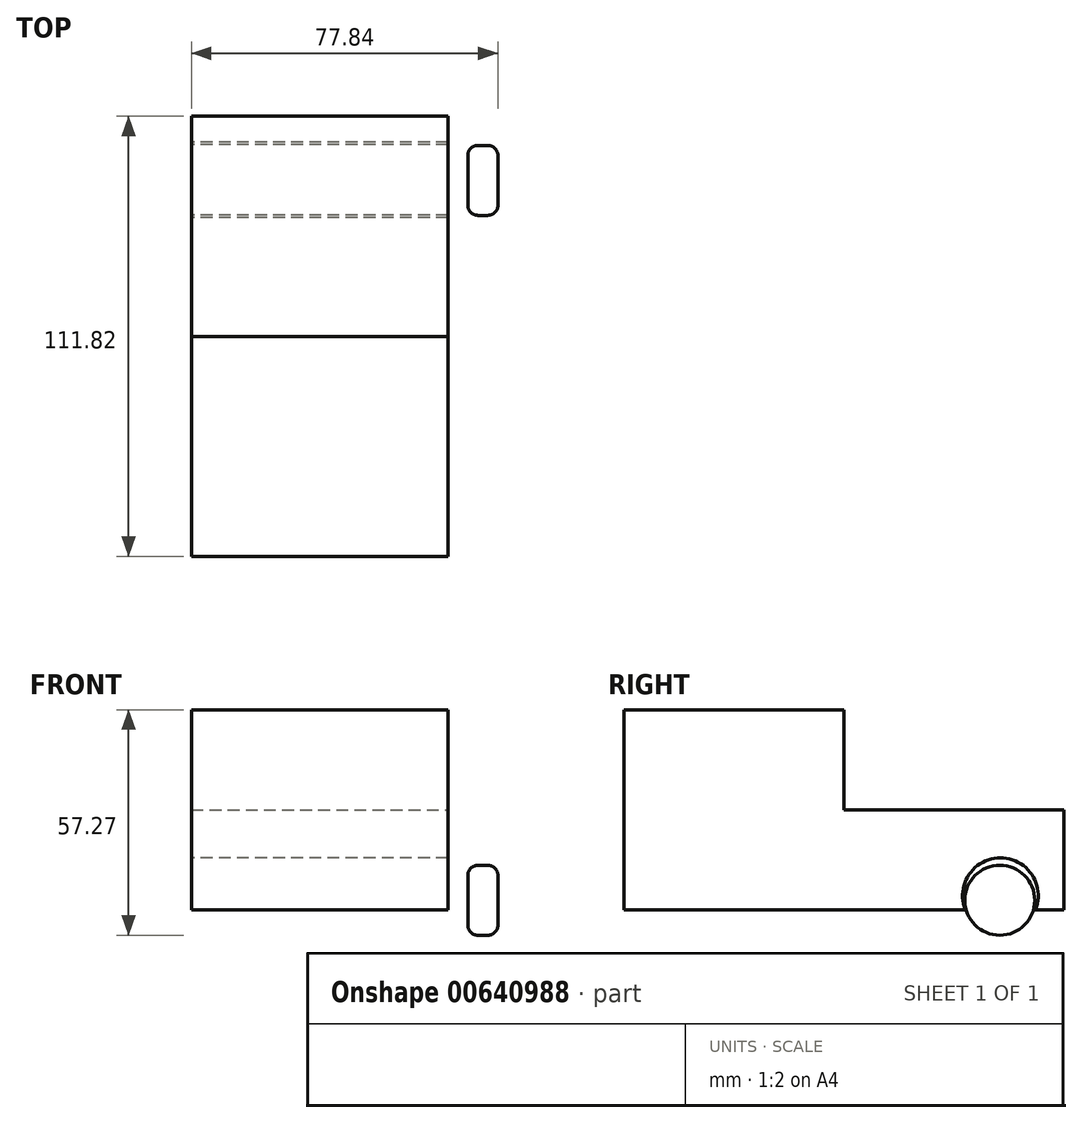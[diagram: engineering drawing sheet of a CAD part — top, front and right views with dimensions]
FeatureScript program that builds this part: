
annotation { "Feature Type Name" : "Feature", "Feature Type Description" : "" }
export const myFeature = defineFeature(function(context is Context, id is Id, definition is map)
    precondition{}
    {
        {
            var Q0;
            Q0=qCreatedBy(makeId("Top.planeOp"),FACE);
            var sketch = newSketch(context, id + "F0", { "sketchPlane" : qUnion([Q0])});
            skLineSegment(sketch, "E0.bottom", {"start": v(-70.22, 55.69) * mm, "end": v(-5.06, 55.69) * mm});
            skLineSegment(sketch, "E0.top", {"start": v(-70.22, -56.13) * mm, "end": v(-5.06, -56.13) * mm});
            skLineSegment(sketch, "E0.left", {"start": v(-70.22, 55.69) * mm, "end": v(-70.22, -56.13) * mm});
            skLineSegment(sketch, "E0.right", {"start": v(-5.06, 55.69) * mm, "end": v(-5.06, -56.13) * mm});
            skSolve(sketch);
        }
        {
            var Q0;
            Q0=makeQuery(id+"F0.imprint","IMPRINT",FACE,{"disambiguationData":[TD([[makeQuery(id+"F0.imprint","IMPRINT",EDGE,{"derivedFrom":sQuery(id+"F0.wireOp",EDGE,"E0.bottom")}),-1.0]])]});
            extrude(context, id + "F1", {"entities" : qUnion([Q0]), "depth" : 25.4 * mm, "offsetDistance" : 25.4 * mm});
        }
        {
            var Q0;
            Q0=makeQuery(id+"F1.opExtrude","CAP_FACE",FACE,{"disambiguationData":[OSD([sQuery(id+"F0.wireOp",EDGE,"E0.bottom"),sQuery(id+"F0.wireOp",EDGE,"E0.top"),sQuery(id+"F0.wireOp",EDGE,"E0.left"),sQuery(id+"F0.wireOp",EDGE,"E0.right")])],"isStart":false});
            var sketch = newSketch(context, id + "F2", { "sketchPlane" : qUnion([Q0])});
            skLineSegment(sketch, "E1.bottom", {"start": v(-70.22, -0.22) * mm, "end": v(-5.06, -0.22) * mm});
            skLineSegment(sketch, "E1.top", {"start": v(-70.22, -56.13) * mm, "end": v(-5.06, -56.13) * mm});
            skLineSegment(sketch, "E1.left", {"start": v(-70.22, -0.22) * mm, "end": v(-70.22, -56.13) * mm});
            skLineSegment(sketch, "E1.right", {"start": v(-5.06, -0.22) * mm, "end": v(-5.06, -56.13) * mm});
            skSolve(sketch);
        }
        {
            var Q0;
            Q0=makeQuery(id+"F2.imprint","IMPRINT",FACE,{"disambiguationData":[TD([[makeQuery(id+"F2.imprint","IMPRINT",EDGE,{"derivedFrom":sQuery(id+"F2.wireOp",EDGE,"E1.bottom")}),-1.0]])]});
            extrude(context, id + "F3", {"entities" : qUnion([Q0]), "operationType" : NewBodyOperationType.ADD, "depth" : 25.4 * mm, "offsetDistance" : 25.4 * mm});
        }
        {
            var Q0;
            Q0=makeQuery(id+"F3.boolean.opBoolean","MERGE",FACE,{"derivedFrom":[makeQuery(id+"F1.opExtrude","SWEPT_FACE",FACE,{"disambiguationData":[OSD([sQuery(id+"F0.wireOp",EDGE,"E0.left")])]}),makeQuery(id+"F3.opExtrude","SWEPT_FACE",FACE,{"disambiguationData":[OSD([sQuery(id+"F2.wireOp",EDGE,"E1.left")])]})]});
            var sketch = newSketch(context, id + "F4", { "sketchPlane" : qUnion([Q0])});
            skCircle(sketch, "E2", {"center": v(-39.53, 3.58) * mm, "radius": 9.61 * mm});
            skSolve(sketch);
        }
        {
            var Q0;
            {var subQ0=sQuery(id+"F4.wireOp",EDGE,"E2");var subQ1=makeQuery(id+"F1.opExtrude","CAP_EDGE",EDGE,{"disambiguationData":[OSD([sQuery(id+"F0.wireOp",EDGE,"E0.left")])],"isStart":true});var subQ2=makeQuery(id+"F4.imprint","INTERSECT",VERTEX,{"disambiguationData":[OD(0.0)],"derivedFrom":[subQ1,subQ0]});Q0=makeQuery(id+"F4.imprint","IMPRINT",FACE,{"disambiguationData":[TD([[makeQuery(id+"F4.imprint","IMPRINT",EDGE,{"disambiguationData":[TD([[subQ2,-1.0]])],"derivedFrom":subQ0}),1.0]])]});}
            var Q1;
            {var subQ0=sQuery(id+"F4.wireOp",EDGE,"E2");var subQ1=makeQuery(id+"F1.opExtrude","CAP_EDGE",EDGE,{"disambiguationData":[OSD([sQuery(id+"F0.wireOp",EDGE,"E0.left")])],"isStart":true});var subQ2=makeQuery(id+"F4.imprint","INTERSECT",VERTEX,{"disambiguationData":[OD(0.0)],"derivedFrom":[subQ1,subQ0]});Q1=makeQuery(id+"F4.imprint","IMPRINT",FACE,{"disambiguationData":[TD([[makeQuery(id+"F4.imprint","IMPRINT",EDGE,{"disambiguationData":[TD([[subQ2,1.0]])],"derivedFrom":subQ0}),1.0]])]});}
            extrude(context, id + "F5", {"entities" : qUnion([Q0, Q1]), "operationType" : NewBodyOperationType.REMOVE, "oppositeDirection" : true, "depth" : 76.2 * mm, "offsetDistance" : 25.4 * mm});
        }
        {
            var Q0;
            Q0=qCreatedBy(makeId("Right.planeOp"),FACE);
            var sketch = newSketch(context, id + "F6", { "sketchPlane" : qUnion([Q0])});
            skCircle(sketch, "E3", {"center": v(39.4, 2.42) * mm, "radius": 8.9 * mm});
            skSolve(sketch);
        }
        {
            var Q0;
            Q0=makeQuery(id+"F6.imprint","IMPRINT",FACE,{"disambiguationData":[TD([[makeQuery(id+"F6.imprint","IMPRINT",EDGE,{"derivedFrom":sQuery(id+"F6.wireOp",EDGE,"E3")}),1.0]])]});
            extrude(context, id + "F7", {"entities" : qUnion([Q0]), "depth" : 7.62 * mm, "offsetDistance" : 25.4 * mm});
        }
        {
            var Q0;
            Q0=makeQuery(id+"F7.opExtrude","CAP_FACE",FACE,{"disambiguationData":[OSD([sQuery(id+"F6.wireOp",EDGE,"E3")])],"isStart":false});
            var Q1;
            Q1=makeQuery(id+"F7.opExtrude","CAP_EDGE",EDGE,{"disambiguationData":[OSD([sQuery(id+"F6.wireOp",EDGE,"E3")])],"isStart":true});
            fillet(context, id + "F8", {"entities" : qUnion([Q0, Q1]), "radius" : 2.54 * mm, "tangentPropagation" : true, "allowEdgeOverflow" : false});
        }
    });
